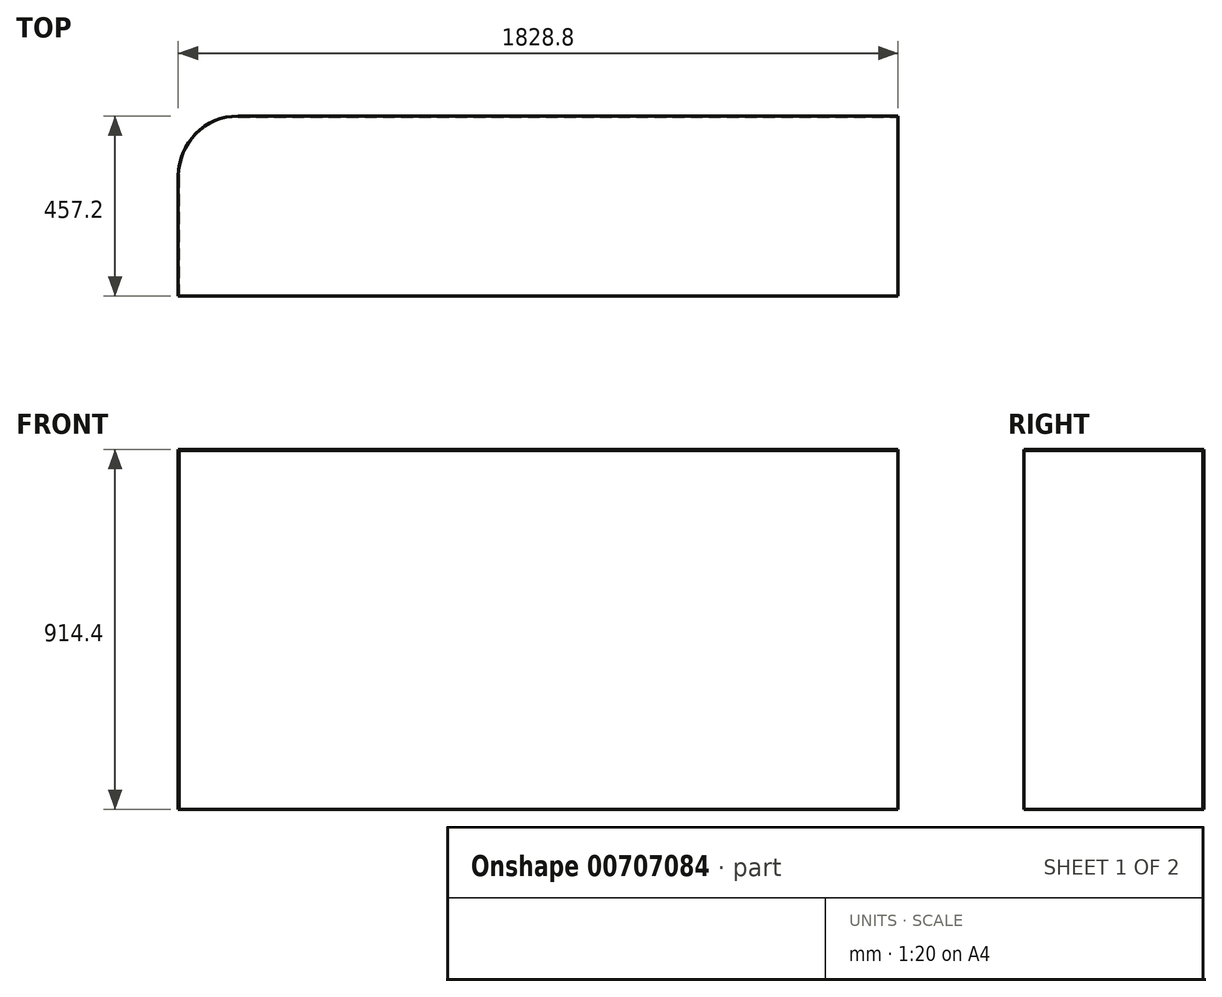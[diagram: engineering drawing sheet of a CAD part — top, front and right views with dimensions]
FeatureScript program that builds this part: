
annotation { "Feature Type Name" : "Feature", "Feature Type Description" : "" }
export const myFeature = defineFeature(function(context is Context, id is Id, definition is map)
    precondition{}
    {
        {
            var Q0;
            Q0=qCreatedBy(makeId("Top.planeOp"),FACE);
            var sketch = newSketch(context, id + "F0", { "sketchPlane" : qUnion([Q0])});
            skLineSegment(sketch, "E0.bottom", {"start": v(-993.96, 631.64) * mm, "end": v(682.75, 631.64) * mm});
            skLineSegment(sketch, "E0.top", {"start": v(-1146.05, 174.44) * mm, "end": v(682.75, 174.44) * mm});
            skLineSegment(sketch, "E0.left", {"start": v(-1146.05, 479.55) * mm, "end": v(-1146.05, 174.44) * mm});
            skLineSegment(sketch, "E0.right", {"start": v(682.75, 631.64) * mm, "end": v(682.75, 174.44) * mm});
            skLineSegment(sketch, "E1.bottom", {"start": v(-1146.05, 174.44) * mm, "end": v(-688.85, 174.44) * mm});
            skLineSegment(sketch, "E1.top", {"start": v(-1146.05, -739.96) * mm, "end": v(-688.85, -739.96) * mm});
            skLineSegment(sketch, "E1.left", {"start": v(-1146.05, 174.44) * mm, "end": v(-1146.05, -739.96) * mm});
            skLineSegment(sketch, "E1.right", {"start": v(-688.85, 174.44) * mm, "end": v(-688.85, -739.96) * mm});
            skPoint(sketch, "E2.visualSharp", {"position": v(-1146.05, 631.64) * mm});
            skArc(sketch, "E2.filletArc", {"start": v(-993.96, 631.64) * mm, "mid": v(-1101.5, 587.1) * mm, "end": v(-1146.05, 479.55) * mm});
            skSolve(sketch);
        }
        {
            var Q0;
            Q0=makeQuery(id+"F0.imprint","IMPRINT",FACE,{"disambiguationData":[TD([[makeQuery(id+"F0.imprint","IMPRINT",EDGE,{"derivedFrom":sQuery(id+"F0.wireOp",EDGE,"E0.bottom")}),-1.0]])]});
            var Q1;
            Q1=makeQuery(id+"F0.imprint","IMPRINT",FACE,{"disambiguationData":[TD([[makeQuery(id+"F0.imprint","IMPRINT",EDGE,{"derivedFrom":sQuery(id+"F0.wireOp",EDGE,"E1.bottom")}),-1.0]])]});
            extrude(context, id + "F1", {"entities" : qUnion([Q0, Q1]), "depth" : 914.4 * mm});
        }
        {
            var Q0;
            Q0=makeQuery(id+"F1.opExtrude","SWEPT_FACE",FACE,{"disambiguationData":[OSD([sQuery(id+"F0.wireOp",EDGE,"E0.top")])]});
            var Q1;
            Q1=makeQuery(id+"F1.opExtrude","SWEPT_FACE",FACE,{"disambiguationData":[OSD([sQuery(id+"F0.wireOp",EDGE,"E0.right")])]});
            var Q2;
            Q2=makeQuery(id+"F1.opExtrude","SWEPT_FACE",FACE,{"disambiguationData":[OSD([sQuery(id+"F0.wireOp",EDGE,"E1.top")])]});
            var Q3;
            Q3=makeQuery(id+"F1.opExtrude","SWEPT_FACE",FACE,{"disambiguationData":[OSD([sQuery(id+"F0.wireOp",EDGE,"E1.right")])]});
            var Q4;
            Q4=makeQuery(id+"F1.opExtrude","CAP_FACE",FACE,{"disambiguationData":[OSD([sQuery(id+"F0.wireOp",EDGE,"E0.bottom"),sQuery(id+"F0.wireOp",EDGE,"E0.top"),sQuery(id+"F0.wireOp",EDGE,"E0.left"),sQuery(id+"F0.wireOp",EDGE,"E0.right"),sQuery(id+"F0.wireOp",EDGE,"E1.top"),sQuery(id+"F0.wireOp",EDGE,"E1.left"),sQuery(id+"F0.wireOp",EDGE,"E1.right"),sQuery(id+"F0.wireOp",EDGE,"E2.filletArc")])],"isStart":true});
            shell(context, id + "F2", {"entities" : qUnion([Q0, Q1, Q2, Q3, Q4]), "thickness" : 2.54 * mm});
        }
    });
